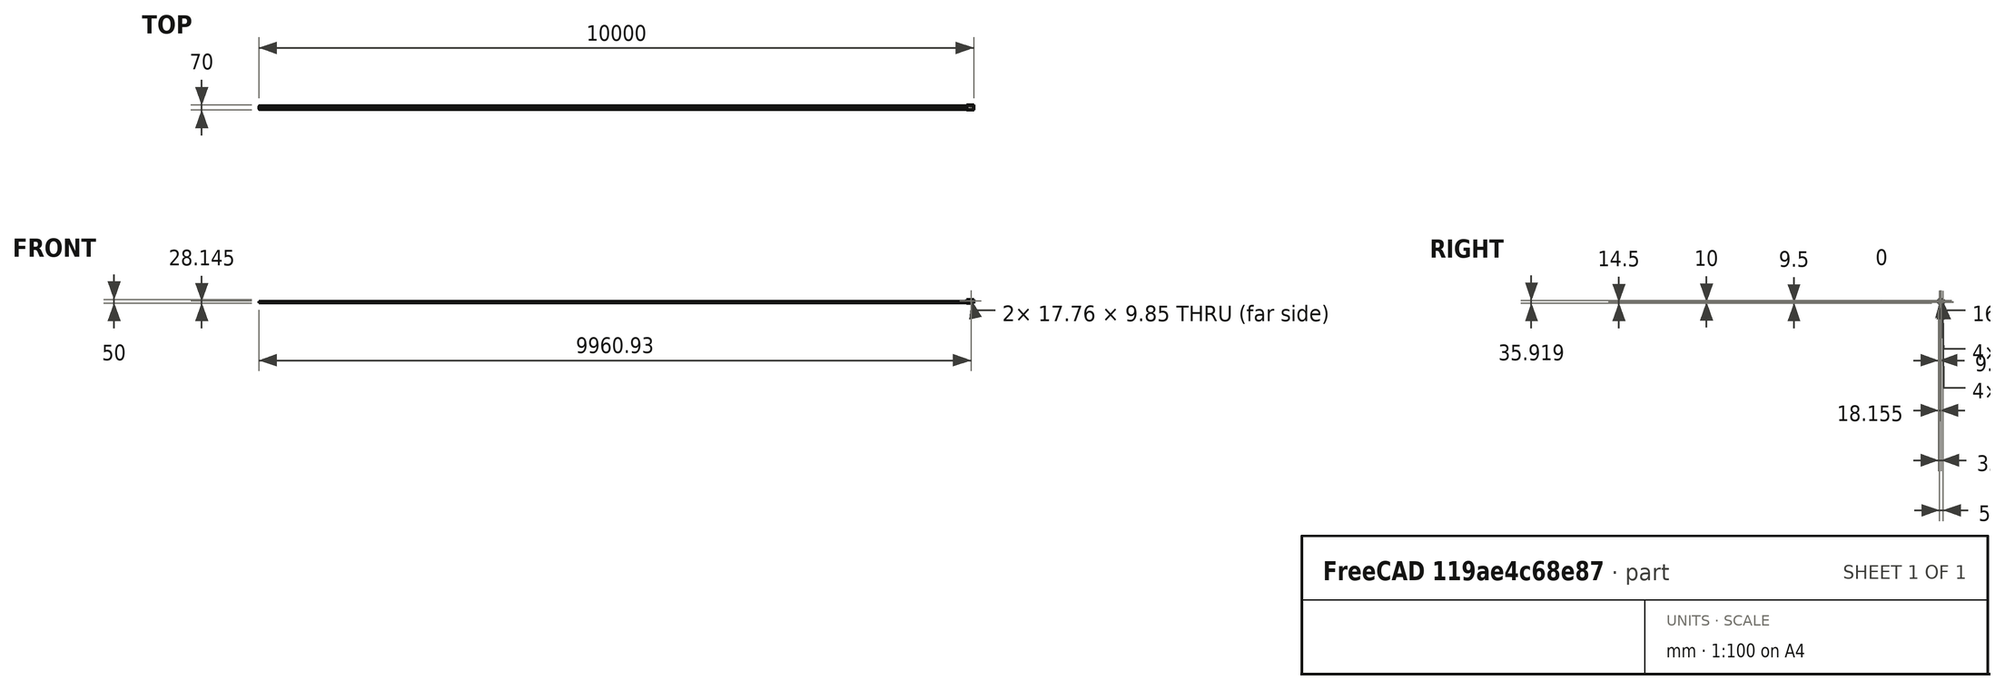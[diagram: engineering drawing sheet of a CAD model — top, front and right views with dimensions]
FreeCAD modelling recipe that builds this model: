
FCSTD DOCUMENT  (FreeCAD 0.16R6707 (Git))
Label: cuerpo
License: All rights reserved
LicenseURL: http://en.wikipedia.org/wiki/All_rights_reserved
objects: Sketcher::SketchObject×10, PartDesign::Pocket×9, Mesh::Feature×4, PartDesign::Chamfer×4, Part::Box×1, PartDesign::Pad×1, Part::Feature×1
note: 36 computed .brp shape members not serialized (recipe doc carries the construction recipe); baked Part::Feature solids carry a one-line shape summary decoded from their .brp

FEATURE [Part::Box] Box  label="Cubo"
  Height = 50
  Length = 100
  Width = 70
FEATURE [Sketcher::SketchObject] Sketch
  ExternalGeometry = -> [Box]
  Placement = pos=(0,0,50) rot=(0,0,1;0rad)
  Support = -> Box [Face6]
  sketch-geometry (4):
    g0: LineSegment StartX=3 StartY=67 StartZ=0 EndX=97 EndY=67 EndZ=0
    g1: LineSegment StartX=97 StartY=67 StartZ=0 EndX=97 EndY=3 EndZ=0
    g2: LineSegment StartX=97 StartY=3 StartZ=0 EndX=3 EndY=3 EndZ=0
    g3: LineSegment StartX=3 StartY=3 StartZ=0 EndX=3 EndY=67 EndZ=0
  constraints (12):
    c: Coincident(g0,g1)
    c: Coincident(g1,g2)
    c: Coincident(g2,g3)
    c: Coincident(g3,g0)
    c: Horizontal(g0)
    c: Horizontal(g2)
    c: Vertical(g1)
    c: Vertical(g3)
    c: DistanceY(g-1,g2) = 3
    c: DistanceX(g-2,g0) = 3
    c: Distance(g1,g-3) = 3
    c: Distance(g0,g-4) = 3
FEATURE [PartDesign::Pocket] Pocket
  Length = 47
  Sketch = -> Sketch
  Type = 0
FEATURE [Mesh::Feature] rPi2_01
  Placement = pos=(8,6,28) rot=(0,0,1;0rad)
FEATURE [Mesh::Feature] Parallax_servo_repaired
  Placement = pos=(73,7,4) rot=(0.57735,0.57735,0.57735;2.0944rad)
FEATURE [Mesh::Feature] Parallax_servo_repaired001
  Placement = pos=(27,10,24) rot=(0.57735,0.57735,-0.57735;4.18879rad)
FEATURE [Sketcher::SketchObject] Sketch001
  Placement = pos=(100,0,0) rot=(0.57735,0.57735,0.57735;2.0944rad)
  Support = -> Pocket [Face6]
  sketch-geometry (12):
    g0: LineSegment StartX=14 StartY=25 StartZ=0 EndX=56.2098 EndY=25 EndZ=0
    g1: LineSegment StartX=56.2098 StartY=25 StartZ=0 EndX=56.2098 EndY=4 EndZ=0
    g2: LineSegment StartX=56.2098 StartY=4 StartZ=0 EndX=14 EndY=4 EndZ=0
    g3: LineSegment StartX=14 StartY=4 StartZ=0 EndX=14 EndY=25 EndZ=0
    g4: Circle CenterX=59.7909 CenterY=19.5 CenterZ=0 NormalX=0 NormalY=0 NormalZ=1 Radius=2.5
    g5: Circle CenterX=59.7909 CenterY=9.5 CenterZ=0 NormalX=0 NormalY=0 NormalZ=1 Radius=2.5
    g6: Circle CenterX=9.48711 CenterY=19.5 CenterZ=0 NormalX=0 NormalY=0 NormalZ=1 Radius=2.5
    g7: Circle CenterX=9.48711 CenterY=9.5 CenterZ=0 NormalX=0 NormalY=0 NormalZ=1 Radius=2.5
    g8: LineSegment [constr] StartX=9.48711 StartY=19.5 StartZ=0 EndX=59.7909 EndY=19.5 EndZ=0
    g9: LineSegment [constr] StartX=59.7909 StartY=19.5 StartZ=0 EndX=59.7909 EndY=9.5 EndZ=0
    g10: LineSegment [constr] StartX=59.7909 StartY=9.5 StartZ=0 EndX=9.48711 EndY=9.5 EndZ=0
    g11: LineSegment [constr] StartX=9.48711 StartY=9.5 StartZ=0 EndX=9.48711 EndY=19.5 EndZ=0
  constraints (32):
    c: Coincident(g0,g1)
    c: Coincident(g1,g2)
    c: Coincident(g2,g3)
    c: Coincident(g3,g0)
    c: Horizontal(g0)
    c: Horizontal(g2)
    c: Vertical(g1)
    c: Vertical(g3)
    c: DistanceX(g0,g0) = 42.2098
    c: DistanceY(g1,g1) = 21
    c: DistanceX(g-2,g0) = 14
    c: DistanceY(g-1,g1) = 4
    c: Coincident(g8,g9)
    c: Coincident(g9,g10)
    c: Coincident(g10,g11)
    c: Coincident(g11,g8)
    c: Horizontal(g8)
    c: Horizontal(g10)
    c: Vertical(g9)
    c: Vertical(g11)
    c: Coincident(g8,g6)
    c: Coincident(g10,g7)
    c: Coincident(g4,g8)
    c: Coincident(g5,g9)
    c: Equal(g6,g7)
    c: Equal(g7,g5)
    c: Equal(g5,g4)
    c: Radius(g4) = 2.5
    c: DistanceY(g11,g11) = 10
    c: DistanceX(g10,g10) = 50.3038
    c: DistanceX(g-2,g6) = 9.48711
    c: Distance(g2,g10) = 5.5
FEATURE [PartDesign::Pocket] Pocket001
  Length = 5
  Sketch = -> Sketch001
  Type = 1
FEATURE [Sketcher::SketchObject] Sketch002
  ExternalGeometry = -> [Pocket001]
  Placement = pos=(0,0,0) rot=(1,0,0;3.14159rad)
  Support = -> Pocket001 [Face4]
  sketch-geometry (8):
    g0: Circle CenterX=31.5896 CenterY=-9.6912 CenterZ=0 NormalX=0 NormalY=0 NormalZ=1 Radius=1.76
    g1: Circle CenterX=31.5896 CenterY=-58.4261 CenterZ=0 NormalX=0 NormalY=0 NormalZ=1 Radius=1.76
    g2: Circle CenterX=89.4043 CenterY=-9.6912 CenterZ=0 NormalX=0 NormalY=0 NormalZ=1 Radius=1.76
    g3: Circle CenterX=89.4043 CenterY=-58.4261 CenterZ=0 NormalX=0 NormalY=0 NormalZ=1 Radius=1.76
    g4: LineSegment [constr] StartX=31.5896 StartY=-9.6912 StartZ=0 EndX=89.4043 EndY=-9.6912 EndZ=0
    g5: LineSegment [constr] StartX=89.4043 StartY=-9.6912 StartZ=0 EndX=89.4043 EndY=-58.4261 EndZ=0
    g6: LineSegment [constr] StartX=89.4043 StartY=-58.4261 StartZ=0 EndX=31.5896 EndY=-58.4261 EndZ=0
    g7: LineSegment [constr] StartX=31.5896 StartY=-58.4261 StartZ=0 EndX=31.5896 EndY=-9.6912 EndZ=0
  constraints (20):
    c: Coincident(g4,g5)
    c: Coincident(g5,g6)
    c: Coincident(g6,g7)
    c: Coincident(g7,g4)
    c: Horizontal(g4)
    c: Horizontal(g6)
    c: Vertical(g5)
    c: Vertical(g7)
    c: Coincident(g0,g4)
    c: Coincident(g1,g6)
    c: Coincident(g4,g2)
    c: Coincident(g3,g5)
    c: Equal(g0,g1)
    c: Equal(g1,g2)
    c: Equal(g2,g3)
    c: Radius(g0) = 1.76
    c: DistanceX(g6,g6) = 57.8147
    c: DistanceY(g7,g7) = 48.7349
    c: DistanceX(g-2,g1) = 31.5896
    c: Distance(g3,g-3) = 11.5739
FEATURE [PartDesign::Pocket] Pocket002
  Length = 5
  Sketch = -> Sketch002
  Type = 0
FEATURE [Sketcher::SketchObject] Sketch003
  Placement = pos=(0,70,0) rot=(0,0.707107,0.707107;3.14159rad)
  Support = -> Pocket002 [Face5]
  sketch-geometry (11):
    g0: LineSegment StartX=-69.8099 StartY=33.072 StartZ=0 EndX=-52.0529 EndY=33.072 EndZ=0
    g1: LineSegment StartX=-52.0529 StartY=33.072 StartZ=0 EndX=-52.0529 EndY=23.2184 EndZ=0
    g2: LineSegment StartX=-52.0529 StartY=23.2184 StartZ=0 EndX=-69.8099 EndY=23.2184 EndZ=0
    g3: LineSegment StartX=-69.8099 StartY=23.2184 StartZ=0 EndX=-69.8099 EndY=33.072 EndZ=0
    g4: Circle CenterX=-39.12 CenterY=28.0425 CenterZ=0 NormalX=0 NormalY=0 NormalZ=1 Radius=3.55709
    g5: LineSegment StartX=-85.3181 StartY=29.0463 StartZ=0 EndX=-79.0594 EndY=29.0463 EndZ=0
    g6: LineSegment StartX=-79.0594 StartY=29.0463 StartZ=0 EndX=-77.4676 EndY=26.3495 EndZ=0
    g7: LineSegment StartX=-77.4676 StartY=26.3495 StartZ=0 EndX=-79.0128 EndY=23.6258 EndZ=0
    g8: LineSegment StartX=-79.0128 StartY=23.6258 StartZ=0 EndX=-85.2714 EndY=23.6258 EndZ=0
    g9: LineSegment StartX=-85.2714 StartY=23.6258 StartZ=0 EndX=-86.8633 EndY=26.3225 EndZ=0
    g10: LineSegment StartX=-86.8633 StartY=26.3225 StartZ=0 EndX=-85.3181 EndY=29.0463 EndZ=0
  constraints (20):
    c: Coincident(g0,g1)
    c: Coincident(g1,g2)
    c: Coincident(g2,g3)
    c: Coincident(g3,g0)
    c: Horizontal(g0)
    c: Horizontal(g2)
    c: Vertical(g1)
    c: Vertical(g3)
    c: Horizontal(g5)
    c: Coincident(g5,g6)
    c: Coincident(g6,g7)
    c: Coincident(g7,g8)
    c: Horizontal(g8)
    c: Coincident(g8,g9)
    c: Coincident(g9,g10)
    c: Coincident(g10,g5)
    c: Equal(g8,g5)
    c: Equal(g10,g9)
    c: Equal(g9,g6)
    c: Equal(g6,g7)
FEATURE [PartDesign::Pocket] Pocket003
  Length = 5
  Sketch = -> Sketch003
  Type = 0
FEATURE [Sketcher::SketchObject] Sketch004
  Placement = pos=(0,0,0) rot=(0.57735,-0.57735,-0.57735;2.0944rad)
  Support = -> Pocket003 [Face1]
  sketch-geometry (14):
    g0: LineSegment StartX=-62.3527 StartY=42.75 StartZ=0 EndX=-45.6122 EndY=42.75 EndZ=0
    g1: LineSegment StartX=-45.6122 StartY=42.75 StartZ=0 EndX=-45.6122 EndY=27.5472 EndZ=0
    g2: LineSegment StartX=-45.6122 StartY=27.5472 StartZ=0 EndX=-62.3527 EndY=27.5472 EndZ=0
    g3: LineSegment StartX=-62.3527 StartY=27.5472 StartZ=0 EndX=-62.3527 EndY=42.75 EndZ=0
    g4: LineSegment StartX=-42.7087 StartY=44.2912 StartZ=0 EndX=-28.2749 EndY=44.2912 EndZ=0
    g5: LineSegment StartX=-28.2749 StartY=44.2912 StartZ=0 EndX=-28.2749 EndY=27.5472 EndZ=0
    g6: LineSegment StartX=-28.2749 StartY=27.5472 StartZ=0 EndX=-42.7087 EndY=27.5472 EndZ=0
    g7: LineSegment StartX=-42.7087 StartY=27.5472 StartZ=0 EndX=-42.7087 EndY=44.2912 EndZ=0
    g8: LineSegment StartX=-25.3714 StartY=44.2912 StartZ=0 EndX=-10.9377 EndY=44.2912 EndZ=0
    g9: LineSegment StartX=-10.9377 StartY=44.2912 StartZ=0 EndX=-10.9377 EndY=27.5472 EndZ=0
    g10: LineSegment StartX=-10.9377 StartY=27.5472 StartZ=0 EndX=-25.3714 EndY=27.5472 EndZ=0
    g11: LineSegment StartX=-25.3714 StartY=27.5472 StartZ=0 EndX=-25.3714 EndY=44.2912 EndZ=0
    g12: LineSegment [constr] StartX=-28.2749 StartY=27.5472 StartZ=0 EndX=-25.3714 EndY=27.5472 EndZ=0
    g13: LineSegment [constr] StartX=-45.6122 StartY=27.5472 StartZ=0 EndX=-42.7087 EndY=27.5472 EndZ=0
  constraints (34):
    c: Coincident(g0,g1)
    c: Coincident(g1,g2)
    c: Coincident(g2,g3)
    c: Coincident(g3,g0)
    c: Horizontal(g0)
    c: Horizontal(g2)
    c: Vertical(g1)
    c: Vertical(g3)
    c: Coincident(g4,g5)
    c: Coincident(g5,g6)
    c: Coincident(g6,g7)
    c: Coincident(g7,g4)
    c: Horizontal(g4)
    c: Horizontal(g6)
    c: Vertical(g5)
    c: Vertical(g7)
    c: Coincident(g8,g9)
    c: Coincident(g9,g10)
    c: Coincident(g10,g11)
    c: Coincident(g11,g8)
    c: Horizontal(g8)
    c: Horizontal(g10)
    c: Vertical(g9)
    c: Vertical(g11)
    c: Equal(g5,g11)
    c: Equal(g4,g8)
    c: Horizontal(g12)
    c: Coincident(g12,g10)
    c: Coincident(g5,g12)
    c: DistanceY(g-1,g9) = 27.5472
    c: Horizontal(g13)
    c: Equal(g13,g12)
    c: Coincident(g13,g6)
    c: Coincident(g1,g13)
FEATURE [PartDesign::Pocket] Pocket004
  Length = 5
  Sketch = -> Sketch004
  Type = 0
FEATURE [Sketcher::SketchObject] Sketch005
  ExternalGeometry = -> [Pocket004]
  Placement = pos=(0,0,50) rot=(0,0,1;0rad)
  Support = -> Pocket004 [Face3]
  sketch-geometry (4):
    g0: Circle CenterX=3.5 CenterY=66.5 CenterZ=0 NormalX=0 NormalY=0 NormalZ=1 Radius=3.5
    g1: Circle CenterX=96.5 CenterY=66.5 CenterZ=0 NormalX=0 NormalY=0 NormalZ=1 Radius=3.5
    g2: Circle CenterX=96.5 CenterY=3.5 CenterZ=0 NormalX=0 NormalY=0 NormalZ=1 Radius=3.5
    g3: Circle CenterX=3.5 CenterY=3.5 CenterZ=0 NormalX=0 NormalY=0 NormalZ=1 Radius=3.5
  constraints (12):
    c: Tangent(g0,g-3)
    c: Tangent(g0,g-2)
    c: Tangent(g1,g-3)
    c: Tangent(g1,g-4)
    c: Tangent(g2,g-4)
    c: Tangent(g2,g-1)
    c: Tangent(g3,g-1)
    c: Tangent(g3,g-2)
    c: Equal(g0,g1)
    c: Equal(g1,g2)
    c: Equal(g2,g3)
    c: Radius(g0) = 3.5
FEATURE [PartDesign::Pad] Pad
  Length = 15
  Length2 = 100
  Reversed = true
  Sketch = -> Sketch005
  Type = 0
FEATURE [PartDesign::Chamfer] Chamfer
  Base = -> Pad [Edge193]
  Size = 3
FEATURE [PartDesign::Chamfer] Chamfer001
  Base = -> Chamfer [Edge108]
  Size = 3
FEATURE [PartDesign::Chamfer] Chamfer002
  Base = -> Chamfer001 [Edge78]
  Size = 3
FEATURE [PartDesign::Chamfer] Chamfer003
  Base = -> Chamfer002 [Edge16]
  Size = 3
FEATURE [Mesh::Feature] Servo_SG90
  Placement = pos=(39,54,17) rot=(-1,0,0;1.5708rad)
FEATURE [Sketcher::SketchObject] Sketch006
  ExternalGeometry = -> [Chamfer003]
  Placement = pos=(0,70,0) rot=(0,0.707107,0.707107;3.14159rad)
  Support = -> Chamfer003 [Face72]
  sketch-geometry (9):
    g0: LineSegment StartX=-62 StartY=17.5 StartZ=0 EndX=-38 EndY=17.5 EndZ=0
    g1: LineSegment StartX=-38 StartY=17.5 StartZ=0 EndX=-38 EndY=4.5 EndZ=0
    g2: LineSegment StartX=-38 StartY=4.5 StartZ=0 EndX=-62 EndY=4.5 EndZ=0
    g3: LineSegment StartX=-62 StartY=4.5 StartZ=0 EndX=-62 EndY=17.5 EndZ=0
    g4: Circle CenterX=-64.5 CenterY=10.7214 CenterZ=0 NormalX=0 NormalY=0 NormalZ=1 Radius=1
    g5: Circle CenterX=-35.5 CenterY=10.7214 CenterZ=0 NormalX=0 NormalY=0 NormalZ=1 Radius=1
    g6: LineSegment [constr] StartX=-100 StartY=10.7214 StartZ=0 EndX=-64.5 EndY=10.7214 EndZ=0
    g7: LineSegment [constr] StartX=0 StartY=10.7214 StartZ=0 EndX=-35.5 EndY=10.7214 EndZ=0
    g8: LineSegment [constr] StartX=-64.5 StartY=10.7214 StartZ=0 EndX=-35.5 EndY=10.7214 EndZ=0
  constraints (26):
    c: Coincident(g0,g1)
    c: Coincident(g1,g2)
    c: Coincident(g2,g3)
    c: Coincident(g3,g0)
    c: Horizontal(g0)
    c: Horizontal(g2)
    c: Vertical(g1)
    c: Vertical(g3)
    c: DistanceX(g2,g2) = 24
    c: DistanceY(g1,g1) = 13
    c: Horizontal(g6)
    c: Horizontal(g7)
    c: PointOnObject(g7,g-2)
    c: Horizontal(g8)
    c: Equal(g6,g7)
    c: Distance(g5,g1) = 2.5
    c: Coincident(g7,g5)
    c: Coincident(g8,g5)
    c: Coincident(g8,g4)
    c: Coincident(g6,g4)
    c: PointOnObject(g6,g-3)
    c: Distance(g4,g3) = 2.5
    c: DistanceY(g-1,g2) = 4.5
    c: Distance(g-1,g7) = 10.7214
    c: Equal(g5,g4)
    c: Radius(g5) = 1
FEATURE [PartDesign::Pocket] Pocket005
  Length = 5
  Sketch = -> Sketch006
  Type = 0
FEATURE [Sketcher::SketchObject] Sketch007
  ExternalGeometry = -> [Pocket005]
  Placement = pos=(0,0,0) rot=(1,0,0;1.5708rad)
  Support = -> Pocket005 [Face83]
  sketch-geometry (3):
    g0: LineSegment [constr] StartX=0 StartY=50 StartZ=0 EndX=100 EndY=0 EndZ=0
    g1: LineSegment [constr] StartX=100 StartY=50 StartZ=0 EndX=0 EndY=0 EndZ=0
    g2: Circle CenterX=50 CenterY=25 CenterZ=0 NormalX=0 NormalY=0 NormalZ=1 Radius=5
  constraints (7):
    c: Coincident(g0,g-4)
    c: Coincident(g1,g-6)
    c: Coincident(g0,g-6)
    c: Coincident(g1,g-1)
    c: PointOnObject(g2,g1)
    c: PointOnObject(g2,g0)
    c: Radius(g2) = 5
FEATURE [PartDesign::Pocket] Pocket006
  Length = 5
  Sketch = -> Sketch007
  Type = 0
FEATURE [Part::Feature] Pocket006001  label="Pocket007"
  shape: bbox 100 x 70 x 50 mm, 73 faces (baked)
FEATURE [Sketcher::SketchObject] Sketch008
  ExternalGeometry = -> [Pocket006001]
  Placement = pos=(0,0,50) rot=(0,0,1;0rad)
  Support = -> Pocket006001 [Face71]
  sketch-geometry (4):
    g0: Circle CenterX=3.5 CenterY=66.5 CenterZ=0 NormalX=0 NormalY=0 NormalZ=1 Radius=1.75
    g1: Circle CenterX=3.5 CenterY=3.5 CenterZ=0 NormalX=0 NormalY=0 NormalZ=1 Radius=1.75
    g2: Circle CenterX=96.5 CenterY=3.5 CenterZ=0 NormalX=0 NormalY=0 NormalZ=1 Radius=1.75
    g3: Circle CenterX=96.5 CenterY=66.5 CenterZ=0 NormalX=0 NormalY=0 NormalZ=1 Radius=1.75
  constraints (8):
    c: Coincident(g-3,g0)
    c: Coincident(g3,g-4)
    c: Coincident(g2,g-5)
    c: Coincident(g-6,g1)
    c: Equal(g0,g3)
    c: Equal(g3,g2)
    c: Equal(g2,g1)
    c: Radius(g1) = 1.75
FEATURE [PartDesign::Pocket] Pocket006002
  Length = 10
  Sketch = -> Sketch008
  Type = 0
FEATURE [Sketcher::SketchObject] Sketch009
  Placement = pos=(0,0,0) rot=(1,0,0;3.14159rad)
  Support = -> Pocket006002 [Face77]
  sketch-geometry (8):
    g0: LineSegment StartX=45 StartY=-15 StartZ=0 EndX=53 EndY=-15 EndZ=0
    g1: LineSegment StartX=53 StartY=-15 StartZ=0 EndX=53 EndY=-50 EndZ=0
    g2: LineSegment StartX=53 StartY=-50 StartZ=0 EndX=45 EndY=-50 EndZ=0
    g3: LineSegment StartX=45 StartY=-50 StartZ=0 EndX=45 EndY=-15 EndZ=0
    g4: LineSegment StartX=62.9975 StartY=-14.7777 StartZ=0 EndX=70.9975 EndY=-14.7777 EndZ=0
    g5: LineSegment StartX=70.9975 StartY=-14.7777 StartZ=0 EndX=70.9975 EndY=-49.7777 EndZ=0
    g6: LineSegment StartX=70.9975 StartY=-49.7777 StartZ=0 EndX=62.9975 EndY=-49.7777 EndZ=0
    g7: LineSegment StartX=62.9975 StartY=-49.7777 StartZ=0 EndX=62.9975 EndY=-14.7777 EndZ=0
  constraints (23):
    c: Coincident(g0,g1)
    c: Coincident(g1,g2)
    c: Coincident(g2,g3)
    c: Coincident(g3,g0)
    c: Horizontal(g0)
    c: Horizontal(g2)
    c: Vertical(g1)
    c: Vertical(g3)
    c: Coincident(g4,g5)
    c: Coincident(g5,g6)
    c: Coincident(g6,g7)
    c: Coincident(g7,g4)
    c: Horizontal(g4)
    c: Horizontal(g6)
    c: Vertical(g5)
    c: Vertical(g7)
    c: Equal(g7,g1)
    c: Equal(g0,g4)
    c: Distance(g1,g6) = 10
    c: DistanceX(g-2,g2) = 45
    c: DistanceY(g-1,g0) = -15
    c: DistanceY(g5,g5) = 35
    c: DistanceX(g6,g6) = 8
FEATURE [PartDesign::Pocket] Pocket006003
  Length = 5
  Sketch = -> Sketch009
  Type = 0
